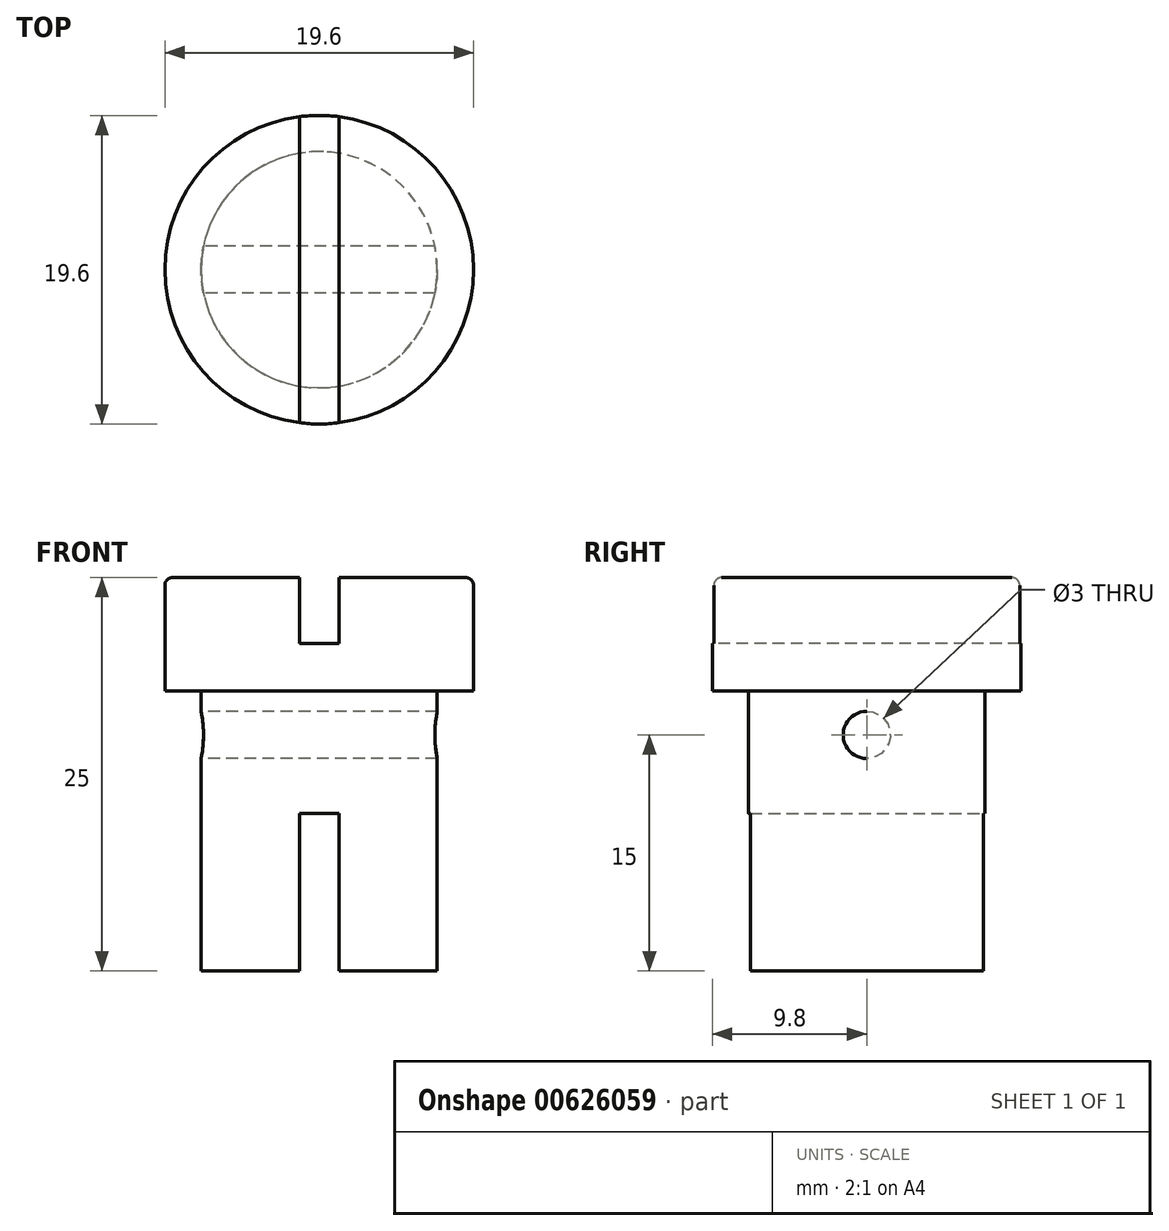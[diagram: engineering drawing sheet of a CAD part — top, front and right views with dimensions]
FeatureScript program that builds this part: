
annotation { "Feature Type Name" : "Feature", "Feature Type Description" : "" }
export const myFeature = defineFeature(function(context is Context, id is Id, definition is map)
    precondition{}
    {
        {
            var Q0;
            Q0=qCreatedBy(makeId("Front.planeOp"),FACE);
            var sketch = newSketch(context, id + "F0", { "sketchPlane" : qUnion([Q0])});
            skLineSegment(sketch, "E0", {"start": v(0, 0) * mm, "end": v(7.5, 0) * mm});
            skLineSegment(sketch, "E1", {"start": v(7.5, 0) * mm, "end": v(7.5, 17.8) * mm});
            skLineSegment(sketch, "E2", {"start": v(7.5, 17.8) * mm, "end": v(9.8, 17.8) * mm});
            skLineSegment(sketch, "E3", {"start": v(9.8, 17.8) * mm, "end": v(9.8, 25) * mm});
            skLineSegment(sketch, "E4", {"start": v(9.8, 25) * mm, "end": v(0, 25) * mm});
            skLineSegment(sketch, "E5", {"start": v(0, 25) * mm, "end": v(0, 0) * mm});
            skSolve(sketch);
        }
        {
            var Q0;
            Q0=makeQuery(id+"F0.imprint","IMPRINT",FACE,{"disambiguationData":[TD([[makeQuery(id+"F0.imprint","IMPRINT",EDGE,{"derivedFrom":sQuery(id+"F0.wireOp",EDGE,"E0")}),1.0]])]});
            var Q1;
            Q1=sQuery(id+"F0.wireOp",EDGE,"E5");
            revolve(context, id + "F1", {"entities" : qUnion([Q0]), "axis" : qUnion([Q1]), "revolveType" : RevolveType.FULL});
        }
        {
            var Q0;
            Q0=makeQuery(id+"F1.opRevolve","SWEPT_FACE",FACE,{"disambiguationData":[OSD([sQuery(id+"F0.wireOp",EDGE,"E4")])]});
            var sketch = newSketch(context, id + "F2", { "sketchPlane" : qUnion([Q0])});
            skLineSegment(sketch, "E6.bottom", {"start": v(-1.25, 15) * mm, "end": v(1.25, 15) * mm});
            skLineSegment(sketch, "E6.top", {"start": v(-1.25, -15) * mm, "end": v(1.25, -15) * mm});
            skLineSegment(sketch, "E6.left", {"start": v(-1.25, 15) * mm, "end": v(-1.25, -15) * mm});
            skLineSegment(sketch, "E6.right", {"start": v(1.25, 15) * mm, "end": v(1.25, -15) * mm});
            skSolve(sketch);
        }
        {
            var Q0;
            {var subQ0=sQuery(id+"F2.wireOp",EDGE,"E6.bottom");Q0=makeQuery(id+"F2.imprint","IMPRINT",FACE,{"disambiguationData":[TD([[makeQuery(id+"F2.imprint","IMPRINT",EDGE,{"derivedFrom":subQ0}),-1.0]])]});}
            var Q1;
            {var subQ0=sQuery(id+"F2.wireOp",EDGE,"E6.left");var subQ1=makeQuery(id+"F1.opRevolve","SWEPT_EDGE",EDGE,{"disambiguationData":[OSD([sQuery(id+"F0.wireOp",EDGE,"E3"),sQuery(id+"F0.wireOp",EDGE,"E4")])]});var subQ2=makeQuery(id+"F2.imprint","INTERSECT",VERTEX,{"disambiguationData":[OD(0.0)],"derivedFrom":[subQ1,subQ0]});Q1=makeQuery(id+"F2.imprint","IMPRINT",FACE,{"disambiguationData":[TD([[makeQuery(id+"F2.imprint","IMPRINT",EDGE,{"disambiguationData":[TD([[subQ2,-1.0]])],"derivedFrom":subQ0}),1.0]])]});}
            var Q2;
            {var subQ0=sQuery(id+"F2.wireOp",EDGE,"E6.top");Q2=makeQuery(id+"F2.imprint","IMPRINT",FACE,{"disambiguationData":[TD([[makeQuery(id+"F2.imprint","IMPRINT",EDGE,{"derivedFrom":subQ0}),1.0]])]});}
            extrude(context, id + "F3", {"entities" : qUnion([Q0, Q1, Q2]), "operationType" : NewBodyOperationType.REMOVE, "oppositeDirection" : true, "depth" : 4.2 * mm, "offsetDistance" : 25 * mm});
        }
        {
            var Q0;
            {var subQ0=sQuery(id+"F0.wireOp",EDGE,"E3");var subQ1=sQuery(id+"F0.wireOp",EDGE,"E4");Q0=makeQuery(id+"F3.boolean.opBoolean","SPLIT",EDGE,{"disambiguationData":[TD([makeQuery(id+"F3.opExtrude","SWEPT_FACE",FACE,{"disambiguationData":[OSD([sQuery(id+"F2.wireOp",EDGE,"E6.left")])]})])],"derivedFrom":makeQuery(id+"F1.opRevolve","SWEPT_EDGE",EDGE,{"disambiguationData":[OSD([subQ0,subQ1])]})});}
            var Q1;
            {var subQ0=sQuery(id+"F0.wireOp",EDGE,"E3");var subQ1=sQuery(id+"F0.wireOp",EDGE,"E4");Q1=makeQuery(id+"F3.boolean.opBoolean","SPLIT",EDGE,{"disambiguationData":[TD([makeQuery(id+"F3.opExtrude","SWEPT_FACE",FACE,{"disambiguationData":[OSD([sQuery(id+"F2.wireOp",EDGE,"E6.right")])]})])],"derivedFrom":makeQuery(id+"F1.opRevolve","SWEPT_EDGE",EDGE,{"disambiguationData":[OSD([subQ0,subQ1])]})});}
            fillet(context, id + "F4", {"entities" : qUnion([Q0, Q1]), "radius" : .5 * mm, "tangentPropagation" : true, "allowEdgeOverflow" : false});
        }
        {
            var Q0;
            Q0=makeQuery(id+"F1.opRevolve","SWEPT_FACE",FACE,{"disambiguationData":[OSD([sQuery(id+"F0.wireOp",EDGE,"E0")])]});
            var sketch = newSketch(context, id + "F5", { "sketchPlane" : qUnion([Q0])});
            skLineSegment(sketch, "E7.bottom", {"start": v(-1.25, 10) * mm, "end": v(1.25, 10) * mm});
            skLineSegment(sketch, "E7.top", {"start": v(-1.25, -10) * mm, "end": v(1.25, -10) * mm});
            skLineSegment(sketch, "E7.left", {"start": v(-1.25, 10) * mm, "end": v(-1.25, -10) * mm});
            skLineSegment(sketch, "E7.right", {"start": v(1.25, 10) * mm, "end": v(1.25, -10) * mm});
            skSolve(sketch);
        }
        {
            var Q0;
            Q0 = qSketchRegion(id + "F5", true);
            extrude(context, id + "F6", {"entities" : qUnion([Q0]), "operationType" : NewBodyOperationType.REMOVE, "oppositeDirection" : true, "depth" : 10 * mm, "offsetDistance" : 25 * mm});
        }
        {
            var Q0;
            Q0=qCreatedBy(makeId("Right.planeOp"),FACE);
            var sketch = newSketch(context, id + "F7", { "sketchPlane" : qUnion([Q0])});
            skCircle(sketch, "E8", {"center": v(0, 15) * mm, "radius": 1.5 * mm});
            skSolve(sketch);
        }
        {
            var Q0;
            Q0 = qSketchRegion(id + "F7", true);
            extrude(context, id + "F8", {"entities" : qUnion([Q0]), "operationType" : NewBodyOperationType.REMOVE, "depth" : 25 * mm, "offsetDistance" : 25 * mm, "symmetric" : true});
        }
    });
